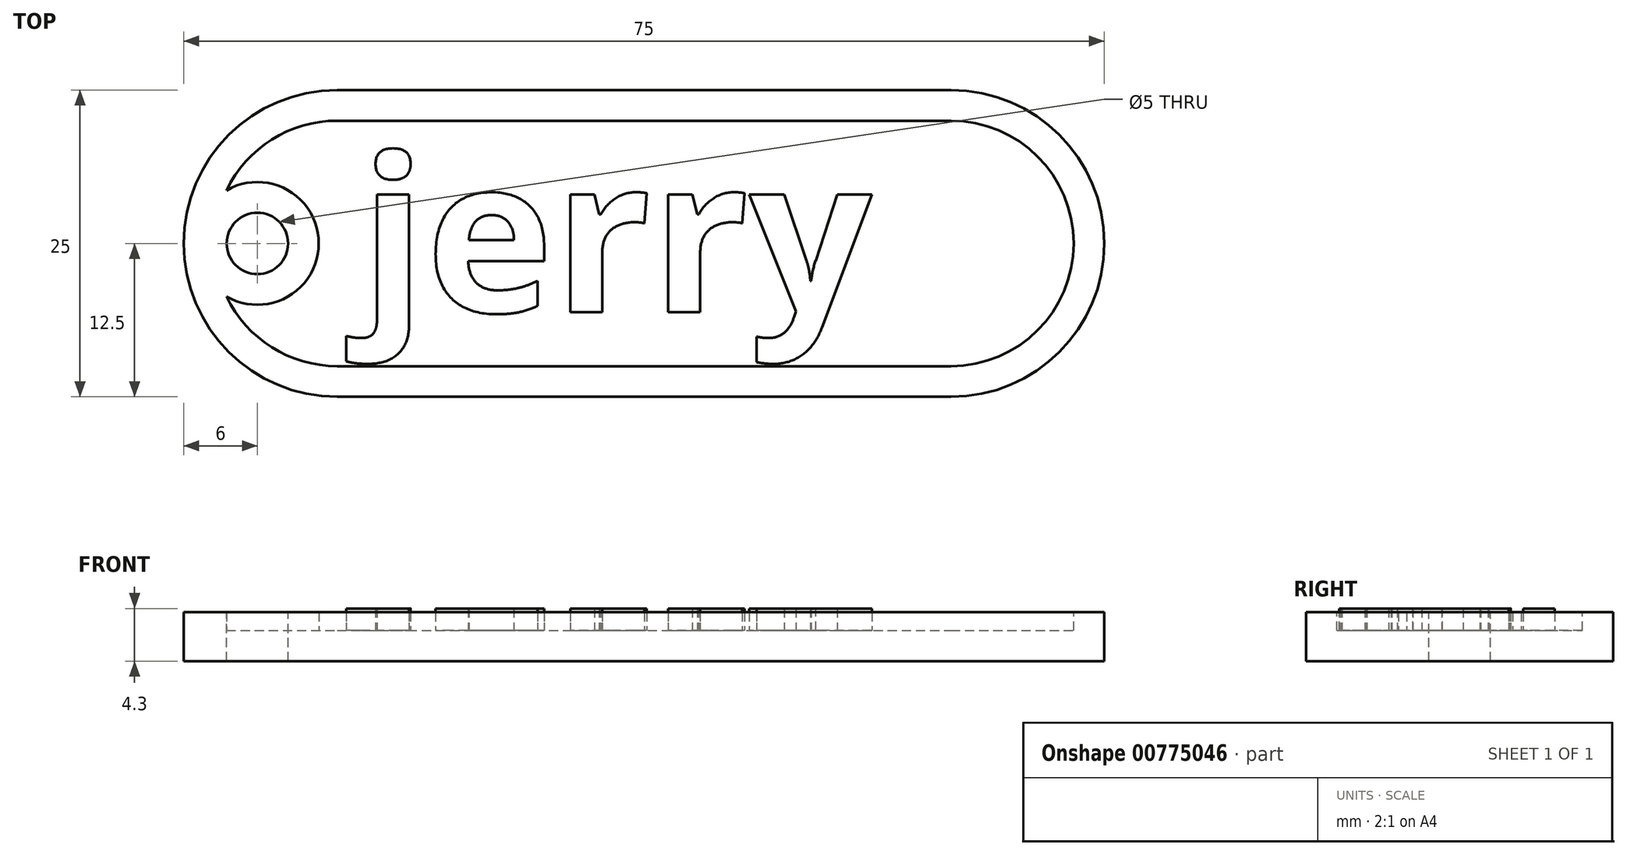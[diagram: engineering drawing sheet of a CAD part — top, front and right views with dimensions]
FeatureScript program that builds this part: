
annotation { "Feature Type Name" : "Feature", "Feature Type Description" : "" }
export const myFeature = defineFeature(function(context is Context, id is Id, definition is map)
    precondition{}
    {
        {
            var Q0;
            Q0=qCreatedBy(makeId("Top.planeOp"),FACE);
            var sketch = newSketch(context, id + "F0", { "sketchPlane" : qUnion([Q0])});
            skLineSegment(sketch, "E0.bottom", {"start": v(12.5, 0) * mm, "end": v(62.5, 0) * mm});
            skLineSegment(sketch, "E0.top", {"start": v(12.5, 25) * mm, "end": v(62.5, 25) * mm});
            skArc(sketch, "E1", {"start": v(12.5, 25) * mm, "mid": v(0, 12.5) * mm, "end": v(12.5, 0) * mm});
            skPoint(sketch, "E1.centerSnap0", {"position": v(0, 12.5) * mm});
            skArc(sketch, "E2", {"start": v(62.5, 0) * mm, "mid": v(75, 12.5) * mm, "end": v(62.5, 25) * mm});
            skPoint(sketch, "E2.centerSnap0", {"position": v(75, 12.5) * mm});
            skPoint(sketch, "E3.orphan", {"position": v(0, 0) * mm});
            skPoint(sketch, "E4.orphan", {"position": v(0, 25) * mm});
            skPoint(sketch, "E5.orphan", {"position": v(75, 25) * mm});
            skPoint(sketch, "E6.orphan", {"position": v(75, 0) * mm});
            skSolve(sketch);
        }
        {
            var Q0;
            Q0=makeQuery(id+"F0.imprint","IMPRINT",FACE,{"disambiguationData":[TD([[makeQuery(id+"F0.imprint","IMPRINT",EDGE,{"derivedFrom":sQuery(id+"F0.wireOp",EDGE,"E0.bottom")}),1.0]])]});
            extrude(context, id + "F1", {"entities" : qUnion([Q0]), "depth" : 4 * mm, "offsetDistance" : 25 * mm});
        }
        {
            var Q0;
            Q0=makeQuery(id+"F1.opExtrude","CAP_FACE",FACE,{"disambiguationData":[OSD([sQuery(id+"F0.wireOp",EDGE,"E0.bottom"),sQuery(id+"F0.wireOp",EDGE,"E0.top"),sQuery(id+"F0.wireOp",EDGE,"E1"),sQuery(id+"F0.wireOp",EDGE,"E2")])],"isStart":false});
            var sketch = newSketch(context, id + "F2", { "sketchPlane" : qUnion([Q0])});
            skArc(sketch, "E7", {"start": v(12.5, 22.5) * mm, "mid": v(2.5, 12.5) * mm, "end": v(12.5, 2.5) * mm});
            skArc(sketch, "E8", {"start": v(62.5, 2.5) * mm, "mid": v(72.5, 12.5) * mm, "end": v(62.5, 22.5) * mm});
            skLineSegment(sketch, "E9", {"start": v(12.5, 22.5) * mm, "end": v(62.5, 22.5) * mm});
            skLineSegment(sketch, "E10", {"start": v(62.5, 2.5) * mm, "end": v(12.5, 2.5) * mm});
            skSolve(sketch);
        }
        {
            var Q0;
            Q0=makeQuery(id+"F2.imprint","IMPRINT",FACE,{"disambiguationData":[TD([[makeQuery(id+"F2.imprint","IMPRINT",EDGE,{"derivedFrom":sQuery(id+"F2.wireOp",EDGE,"E7")}),1.0]])]});
            extrude(context, id + "F3", {"entities" : qUnion([Q0]), "operationType" : NewBodyOperationType.REMOVE, "oppositeDirection" : true, "depth" : 1.5 * mm, "offsetDistance" : 25 * mm});
        }
        {
            var Q0;
            Q0=makeQuery(id+"F3.boolean.opBoolean","COPY",FACE,{"derivedFrom":makeQuery(id+"F3.opExtrude","CAP_FACE",FACE,{"disambiguationData":[OSD([sQuery(id+"F2.wireOp",EDGE,"E7"),sQuery(id+"F2.wireOp",EDGE,"E8"),sQuery(id+"F2.wireOp",EDGE,"E9"),sQuery(id+"F2.wireOp",EDGE,"E10")])],"isStart":false})});
            var sketch = newSketch(context, id + "F4", { "sketchPlane" : qUnion([Q0])});
            skCircle(sketch, "E11", {"center": v(6, 12.5) * mm, "radius": 5 * mm});
            skPoint(sketch, "E11.centerSnap0", {"position": v(2.5, 12.5) * mm});
            skSolve(sketch);
        }
        {
            var Q0;
            {var subQ0=sQuery(id+"F4.wireOp",EDGE,"E11");var subQ1=makeQuery(id+"F3.boolean.opBoolean","COPY",EDGE,{"derivedFrom":makeQuery(id+"F3.opExtrude","CAP_EDGE",EDGE,{"disambiguationData":[OSD([sQuery(id+"F2.wireOp",EDGE,"E7")])],"isStart":false})});var subQ2=makeQuery(id+"F4.imprint","INTERSECT",VERTEX,{"disambiguationData":[OD(0.0)],"derivedFrom":[subQ1,subQ0]});Q0=makeQuery(id+"F4.imprint","IMPRINT",FACE,{"disambiguationData":[TD([[makeQuery(id+"F4.imprint","IMPRINT",EDGE,{"disambiguationData":[TD([[subQ2,1.0]])],"derivedFrom":subQ0}),1.0]])]});}
            var sketch = newSketch(context, id + "F5", { "sketchPlane" : qUnion([Q0])});
            skSolve(sketch);
        }
        {
            var Q0;
            Q0 = qSketchRegion(id + "F5", true);
            var Q1;
            {var subQ0=sQuery(id+"F4.wireOp",EDGE,"E11");var subQ1=makeQuery(id+"F3.boolean.opBoolean","COPY",EDGE,{"derivedFrom":makeQuery(id+"F3.opExtrude","CAP_EDGE",EDGE,{"disambiguationData":[OSD([sQuery(id+"F2.wireOp",EDGE,"E7")])],"isStart":false})});var subQ2=makeQuery(id+"F4.imprint","INTERSECT",VERTEX,{"disambiguationData":[OD(0.0)],"derivedFrom":[subQ1,subQ0]});Q1=makeQuery(id+"F4.imprint","IMPRINT",FACE,{"disambiguationData":[TD([[makeQuery(id+"F4.imprint","IMPRINT",EDGE,{"disambiguationData":[TD([[subQ2,1.0]])],"derivedFrom":subQ0}),1.0]])]});}
            extrude(context, id + "F6", {"entities" : qUnion([Q0, Q1]), "operationType" : NewBodyOperationType.ADD, "depth" : 1.5 * mm, "offsetDistance" : 25 * mm});
        }
        {
            var Q0;
            Q0=makeQuery(id+"F6.boolean.opBoolean","MERGE",FACE,{"derivedFrom":[makeQuery(id+"F1.opExtrude","CAP_FACE",FACE,{"disambiguationData":[OSD([sQuery(id+"F0.wireOp",EDGE,"E0.bottom"),sQuery(id+"F0.wireOp",EDGE,"E0.top"),sQuery(id+"F0.wireOp",EDGE,"E1"),sQuery(id+"F0.wireOp",EDGE,"E2")])],"isStart":false}),makeQuery(id+"F6.opExtrude","CAP_FACE",FACE,{"disambiguationData":[OSD([sQuery(id+"F2.wireOp",EDGE,"E7"),sQuery(id+"F4.wireOp",EDGE,"E11")])],"isStart":false})]});
            var sketch = newSketch(context, id + "F7", { "sketchPlane" : qUnion([Q0])});
            skCircle(sketch, "E12", {"center": v(6, 12.5) * mm, "radius": 2.5 * mm});
            skSolve(sketch);
        }
        {
            var Q0;
            Q0=makeQuery(id+"F7.imprint","IMPRINT",FACE,{"disambiguationData":[TD([[makeQuery(id+"F7.imprint","IMPRINT",EDGE,{"derivedFrom":sQuery(id+"F7.wireOp",EDGE,"E12")}),1.0]])]});
            extrude(context, id + "F8", {"entities" : qUnion([Q0]), "operationType" : NewBodyOperationType.REMOVE, "oppositeDirection" : true, "depth" : 25 * mm, "offsetDistance" : 25 * mm});
        }
        {
            var Q0;
            Q0=makeQuery(id+"F3.boolean.opBoolean","COPY",FACE,{"derivedFrom":makeQuery(id+"F3.opExtrude","CAP_FACE",FACE,{"disambiguationData":[OSD([sQuery(id+"F2.wireOp",EDGE,"E7"),sQuery(id+"F2.wireOp",EDGE,"E8"),sQuery(id+"F2.wireOp",EDGE,"E9"),sQuery(id+"F2.wireOp",EDGE,"E10")])],"isStart":false})});
            var sketch = newSketch(context, id + "F9", { "sketchPlane" : qUnion([Q0])});
            skText(sketch, "E13", { "text": "jerry", "fontName": "OpenSans-Bold.ttf"});
            const initialGuessF9  = {"E13": [0.01437, 0.0069, 1, 0, 0.01265]};
            skSetInitialGuess(sketch, initialGuessF9);
            skSolve(sketch);
        }
        {
            var Q0;
            Q0 = qSketchRegion(id + "F9", true);
            extrude(context, id + "F10", {"entities" : qUnion([Q0]), "operationType" : NewBodyOperationType.ADD, "depth" : 1.8 * mm, "offsetDistance" : 25 * mm});
        }
    });
